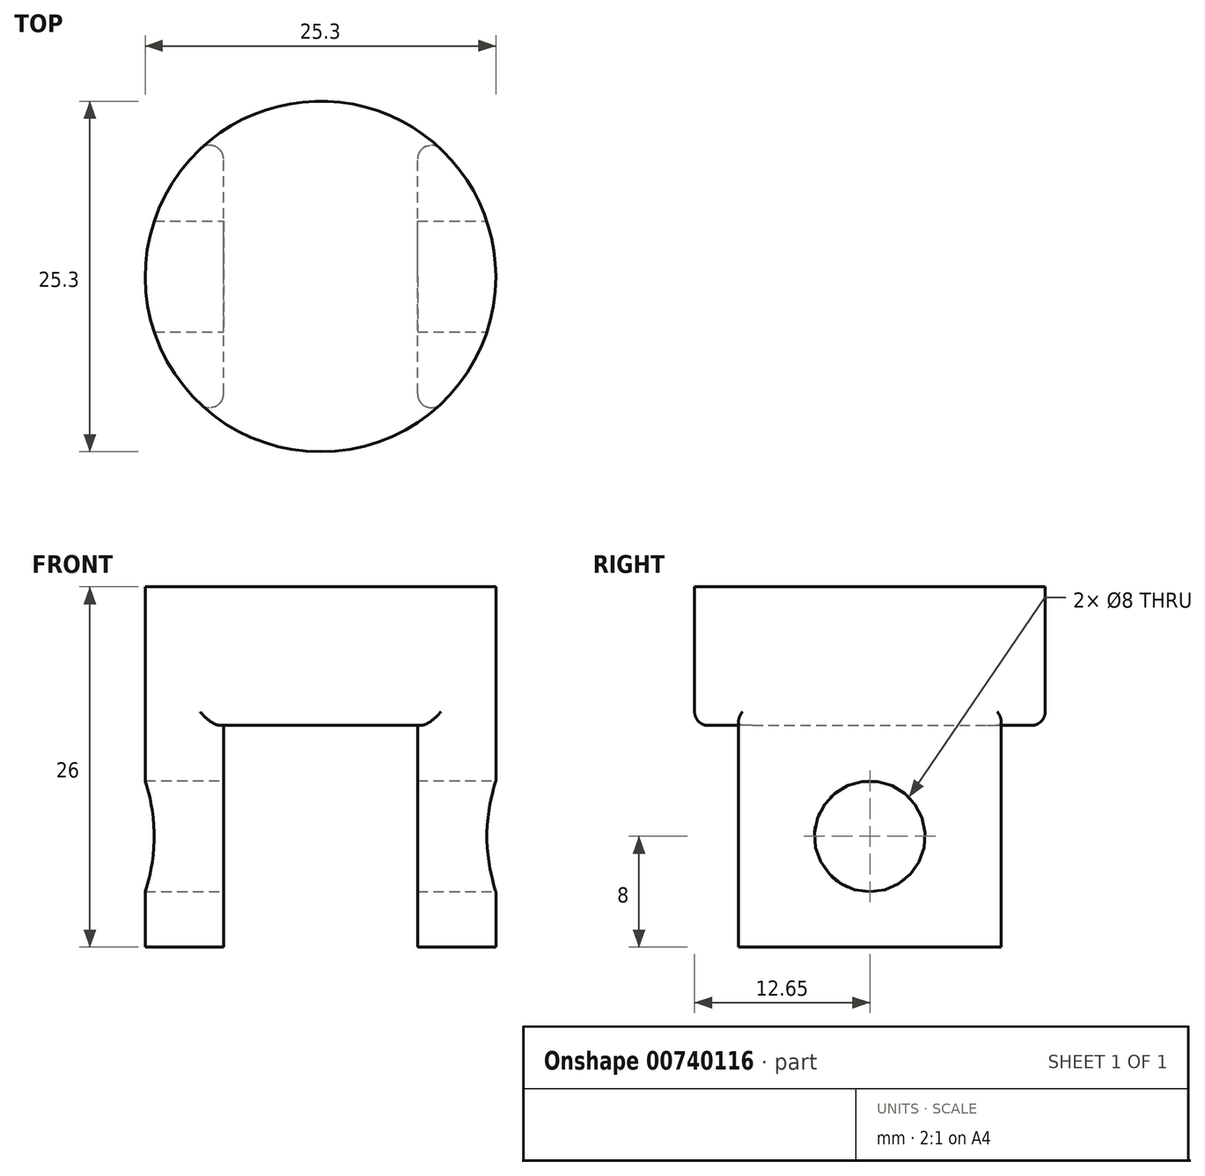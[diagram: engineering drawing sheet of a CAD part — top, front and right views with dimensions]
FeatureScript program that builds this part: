
annotation { "Feature Type Name" : "Feature", "Feature Type Description" : "" }
export const myFeature = defineFeature(function(context is Context, id is Id, definition is map)
    precondition{}
    {
        {
            var Q0;
            Q0=qCreatedBy(makeId("Top.planeOp"),FACE);
            var sketch = newSketch(context, id + "F0", { "sketchPlane" : qUnion([Q0])});
            skCircle(sketch, "E0", {"center": v(0, 0) * mm, "radius": 12.65 * mm});
            skSolve(sketch);
        }
        {
            var Q0;
            Q0 = qSketchRegion(id + "F0", true);
            extrude(context, id + "F1", {"entities" : qUnion([Q0]), "depth" : 26 * mm, "offsetDistance" : 25 * mm});
        }
        {
            var Q0;
            Q0=qCreatedBy(makeId("Top.planeOp"),FACE);
            var sketch = newSketch(context, id + "F2", { "sketchPlane" : qUnion([Q0])});
            skLineSegment(sketch, "E1.bottom", {"start": v(7, -14.68) * mm, "end": v(-7, -14.68) * mm});
            skLineSegment(sketch, "E1.top", {"start": v(7, 14.68) * mm, "end": v(-7, 14.68) * mm});
            skLineSegment(sketch, "E1.left", {"start": v(7, -14.68) * mm, "end": v(7, 14.68) * mm});
            skLineSegment(sketch, "E1.right", {"start": v(-7, -14.68) * mm, "end": v(-7, 14.68) * mm});
            skPoint(sketch, "E1.middle", {"position": v(0, 0) * mm});
            skSolve(sketch);
        }
        {
            var Q0;
            Q0=makeQuery(id+"F2.imprint","IMPRINT",FACE,{"disambiguationData":[TD([[makeQuery(id+"F2.imprint","IMPRINT",EDGE,{"derivedFrom":sQuery(id+"F2.wireOp",EDGE,"E1.bottom")}),-1.0]])]});
            extrude(context, id + "F3", {"entities" : qUnion([Q0]), "operationType" : NewBodyOperationType.REMOVE, "depth" : 16 * mm, "offsetDistance" : 25 * mm});
        }
        {
            var Q0;
            Q0=makeQuery(id+"F3.boolean.opBoolean","INTERSECT",EDGE,{"disambiguationData":[OD(0.0)],"derivedFrom":[makeQuery(id+"F1.opExtrude","SWEPT_FACE",FACE,{"disambiguationData":[OSD([sQuery(id+"F0.wireOp",EDGE,"E0")])]}),makeQuery(id+"F3.opExtrude","SWEPT_FACE",FACE,{"disambiguationData":[OSD([sQuery(id+"F2.wireOp",EDGE,"E1.left")])]})]});
            var Q1;
            Q1=makeQuery(id+"F3.boolean.opBoolean","INTERSECT",EDGE,{"disambiguationData":[OD(0.0)],"derivedFrom":[makeQuery(id+"F1.opExtrude","SWEPT_FACE",FACE,{"disambiguationData":[OSD([sQuery(id+"F0.wireOp",EDGE,"E0")])]}),makeQuery(id+"F3.opExtrude","SWEPT_FACE",FACE,{"disambiguationData":[OSD([sQuery(id+"F2.wireOp",EDGE,"E1.right")])]})]});
            var Q2;
            Q2=makeQuery(id+"F3.boolean.opBoolean","INTERSECT",EDGE,{"disambiguationData":[OD(1.0)],"derivedFrom":[makeQuery(id+"F1.opExtrude","SWEPT_FACE",FACE,{"disambiguationData":[OSD([sQuery(id+"F0.wireOp",EDGE,"E0")])]}),makeQuery(id+"F3.opExtrude","SWEPT_FACE",FACE,{"disambiguationData":[OSD([sQuery(id+"F2.wireOp",EDGE,"E1.left")])]})]});
            var Q3;
            Q3=makeQuery(id+"F3.boolean.opBoolean","INTERSECT",EDGE,{"disambiguationData":[OD(1.0)],"derivedFrom":[makeQuery(id+"F1.opExtrude","SWEPT_FACE",FACE,{"disambiguationData":[OSD([sQuery(id+"F0.wireOp",EDGE,"E0")])]}),makeQuery(id+"F3.opExtrude","SWEPT_FACE",FACE,{"disambiguationData":[OSD([sQuery(id+"F2.wireOp",EDGE,"E1.right")])]})]});
            var Q4;
            Q4=makeQuery(id+"F3.boolean.opBoolean","INTERSECT",EDGE,{"disambiguationData":[OD(0.0)],"derivedFrom":[makeQuery(id+"F1.opExtrude","SWEPT_FACE",FACE,{"disambiguationData":[OSD([sQuery(id+"F0.wireOp",EDGE,"E0")])]}),makeQuery(id+"F3.opExtrude","CAP_FACE",FACE,{"disambiguationData":[OSD([sQuery(id+"F2.wireOp",EDGE,"E1.bottom"),sQuery(id+"F2.wireOp",EDGE,"E1.top"),sQuery(id+"F2.wireOp",EDGE,"E1.left"),sQuery(id+"F2.wireOp",EDGE,"E1.right")])],"isStart":false})]});
            var Q5;
            Q5=makeQuery(id+"F3.boolean.opBoolean","INTERSECT",EDGE,{"disambiguationData":[OD(1.0)],"derivedFrom":[makeQuery(id+"F1.opExtrude","SWEPT_FACE",FACE,{"disambiguationData":[OSD([sQuery(id+"F0.wireOp",EDGE,"E0")])]}),makeQuery(id+"F3.opExtrude","CAP_FACE",FACE,{"disambiguationData":[OSD([sQuery(id+"F2.wireOp",EDGE,"E1.bottom"),sQuery(id+"F2.wireOp",EDGE,"E1.top"),sQuery(id+"F2.wireOp",EDGE,"E1.left"),sQuery(id+"F2.wireOp",EDGE,"E1.right")])],"isStart":false})]});
            fillet(context, id + "F4", {"entities" : qUnion([Q0, Q1, Q2, Q3, Q4, Q5]), "radius" : 1 * mm, "tangentPropagation" : true, "allowEdgeOverflow" : false});
        }
        {
            var Q0;
            Q0=qCreatedBy(makeId("Right.planeOp"),FACE);
            var sketch = newSketch(context, id + "F5", { "sketchPlane" : qUnion([Q0])});
            skCircle(sketch, "E2", {"center": v(0, 8) * mm, "radius": 4 * mm});
            skSolve(sketch);
        }
        {
            var Q0;
            Q0=makeQuery(id+"F5.imprint","IMPRINT",FACE,{"disambiguationData":[TD([[makeQuery(id+"F5.imprint","IMPRINT",EDGE,{"derivedFrom":sQuery(id+"F5.wireOp",EDGE,"E2")}),1.0]])]});
            extrude(context, id + "F6", {"entities" : qUnion([Q0]), "operationType" : NewBodyOperationType.REMOVE, "oppositeDirection" : true, "depth" : 32.4 * mm, "offsetDistance" : 25 * mm, "symmetric" : true});
        }
    });
